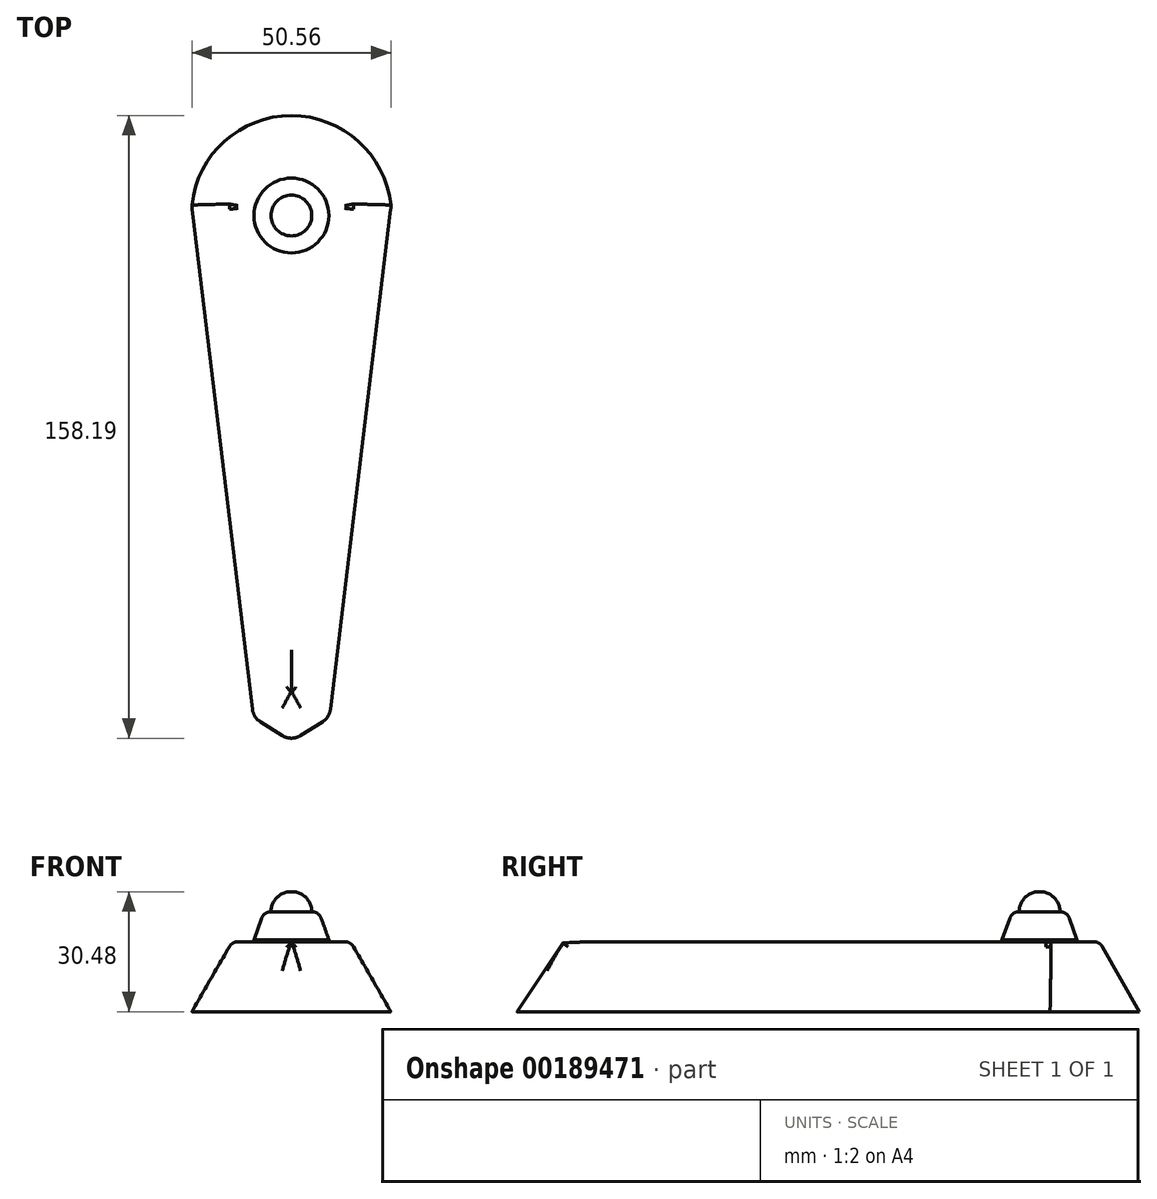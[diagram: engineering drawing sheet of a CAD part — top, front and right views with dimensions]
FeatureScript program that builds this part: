
annotation { "Feature Type Name" : "Feature", "Feature Type Description" : "" }
export const myFeature = defineFeature(function(context is Context, id is Id, definition is map)
    precondition{}
    {
        {
            var Q0;
            Q0=qCreatedBy(makeId("Top.planeOp"),FACE);
            var sketch = newSketch(context, id + "F0", { "sketchPlane" : qUnion([Q0])});
            skArc(sketch, "E0", {"start": v(25.3, 63.5) * mm, "mid": v(0, 86.74) * mm, "end": v(-25.3, 63.5) * mm});
            skLineSegment(sketch, "E1", {"start": v(-25.3, 63.5) * mm, "end": v(-9.65, -66.18) * mm});
            skLineSegment(sketch, "E2", {"start": v(25.3, 63.5) * mm, "end": v(9.65, -66.18) * mm});
            skLineSegment(sketch, "E3", {"start": v(-9.65, -66.18) * mm, "end": v(0, -72.23) * mm});
            skLineSegment(sketch, "E4", {"start": v(9.65, -66.18) * mm, "end": v(0, -72.23) * mm});
            skSolve(sketch);
        }
        {
            var Q0;
            Q0=makeQuery(id+"F0.imprint","IMPRINT",FACE,{"disambiguationData":[TD([[makeQuery(id+"F0.imprint","IMPRINT",EDGE,{"derivedFrom":sQuery(id+"F0.wireOp",EDGE,"E0")}),1.0]])]});
            extrude(context, id + "F1", {"entities" : qUnion([Q0]), "depth" : 17.78 * mm});
        }
        {
            var Q0;
            Q0=makeQuery(id+"F1.opExtrude","CAP_FACE",FACE,{"disambiguationData":[OSD([sQuery(id+"F0.wireOp",EDGE,"E0"),sQuery(id+"F0.wireOp",EDGE,"E1"),sQuery(id+"F0.wireOp",EDGE,"E2"),sQuery(id+"F0.wireOp",EDGE,"E3"),sQuery(id+"F0.wireOp",EDGE,"E4")])],"isStart":false});
            chamfer(context, id + "F2", {"entities" : qUnion([Q0]), "chamferType" : ChamferType.TWO_OFFSETS, "width1" : 10.16 * mm, "oppositeDirection" : false, "width2" : 17.78 * mm, "tangentPropagation" : true});
        }
        {
            var Q0;
            Q0=makeQuery(id+"F2.opChamfer","BLEND_EDGE",EDGE,{"blendedFrom":[makeQuery(id+"F1.opExtrude","CAP_EDGE",EDGE,{"disambiguationData":[OSD([sQuery(id+"F0.wireOp",EDGE,"E2")])],"isStart":false}),makeQuery(id+"F1.opExtrude","CAP_EDGE",EDGE,{"disambiguationData":[OSD([sQuery(id+"F0.wireOp",EDGE,"E4")])],"isStart":false})],"blendedInto":[]});
            var Q1;
            Q1=makeQuery(id+"F2.opChamfer","BLEND_EDGE",EDGE,{"blendedFrom":[makeQuery(id+"F1.opExtrude","CAP_EDGE",EDGE,{"disambiguationData":[OSD([sQuery(id+"F0.wireOp",EDGE,"E3")])],"isStart":false}),makeQuery(id+"F1.opExtrude","CAP_EDGE",EDGE,{"disambiguationData":[OSD([sQuery(id+"F0.wireOp",EDGE,"E4")])],"isStart":false})],"blendedInto":[]});
            var Q2;
            Q2=makeQuery(id+"F2.opChamfer","BLEND_EDGE",EDGE,{"blendedFrom":[makeQuery(id+"F1.opExtrude","CAP_EDGE",EDGE,{"disambiguationData":[OSD([sQuery(id+"F0.wireOp",EDGE,"E0")])],"isStart":false}),makeQuery(id+"F1.opExtrude","CAP_EDGE",EDGE,{"disambiguationData":[OSD([sQuery(id+"F0.wireOp",EDGE,"E2")])],"isStart":false})],"blendedInto":[]});
            var Q3;
            Q3=makeQuery(id+"F2.opChamfer","BLEND_EDGE",EDGE,{"blendedFrom":[makeQuery(id+"F1.opExtrude","CAP_EDGE",EDGE,{"disambiguationData":[OSD([sQuery(id+"F0.wireOp",EDGE,"E1")])],"isStart":false}),makeQuery(id+"F1.opExtrude","CAP_EDGE",EDGE,{"disambiguationData":[OSD([sQuery(id+"F0.wireOp",EDGE,"E3")])],"isStart":false})],"blendedInto":[]});
            var Q4;
            Q4=makeQuery(id+"F2.opChamfer","BLEND_EDGE",EDGE,{"blendedFrom":[makeQuery(id+"F1.opExtrude","CAP_EDGE",EDGE,{"disambiguationData":[OSD([sQuery(id+"F0.wireOp",EDGE,"E0")])],"isStart":false}),makeQuery(id+"F1.opExtrude","CAP_EDGE",EDGE,{"disambiguationData":[OSD([sQuery(id+"F0.wireOp",EDGE,"E1")])],"isStart":false})],"blendedInto":[]});
            fillet(context, id + "F3", {"entities" : qUnion([Q0, Q1, Q2, Q3, Q4]), "radius" : 5.08 * mm, "tangentPropagation" : true, "allowEdgeOverflow" : false});
        }
        {
            var Q0;
            Q0=makeQuery(id+"F1.opExtrude","CAP_FACE",FACE,{"disambiguationData":[OSD([sQuery(id+"F0.wireOp",EDGE,"E0"),sQuery(id+"F0.wireOp",EDGE,"E1"),sQuery(id+"F0.wireOp",EDGE,"E2"),sQuery(id+"F0.wireOp",EDGE,"E3"),sQuery(id+"F0.wireOp",EDGE,"E4")])],"isStart":false});
            fillet(context, id + "F4", {"entities" : qUnion([Q0]), "radius" : 2.54 * mm, "tangentPropagation" : true, "allowEdgeOverflow" : false});
        }
        {
            var Q0;
            Q0=makeQuery(id+"F1.opExtrude","CAP_FACE",FACE,{"disambiguationData":[OSD([sQuery(id+"F0.wireOp",EDGE,"E0"),sQuery(id+"F0.wireOp",EDGE,"E1"),sQuery(id+"F0.wireOp",EDGE,"E2"),sQuery(id+"F0.wireOp",EDGE,"E3"),sQuery(id+"F0.wireOp",EDGE,"E4")])],"isStart":false});
            var sketch = newSketch(context, id + "F5", { "sketchPlane" : qUnion([Q0])});
            skCircle(sketch, "E5", {"center": v(0, 61.34) * mm, "radius": 9.5 * mm});
            skSolve(sketch);
        }
        {
            var Q0;
            Q0 = qSketchRegion(id + "F5", true);
            extrude(context, id + "F6", {"entities" : qUnion([Q0]), "operationType" : NewBodyOperationType.ADD, "depth" : 7.62 * mm});
        }
        {
            var Q0;
            Q0=makeQuery(id+"F6.opExtrude","CAP_FACE",FACE,{"disambiguationData":[OSD([sQuery(id+"F5.wireOp",EDGE,"E5")])],"isStart":false});
            chamfer(context, id + "F7", {"entities" : qUnion([Q0]), "chamferType" : ChamferType.TWO_OFFSETS, "width1" : 2.54 * mm, "oppositeDirection" : false, "width2" : 7.11 * mm, "tangentPropagation" : true});
        }
        {
            var Q0;
            Q0=makeQuery(id+"F6.opExtrude","CAP_FACE",FACE,{"disambiguationData":[OSD([sQuery(id+"F5.wireOp",EDGE,"E5")])],"isStart":false});
            fillet(context, id + "F8", {"entities" : qUnion([Q0]), "radius" : 2.54 * mm, "tangentPropagation" : true, "allowEdgeOverflow" : false});
        }
        {
            var Q0;
            Q0=makeQuery(id+"F6.opExtrude","CAP_FACE",FACE,{"disambiguationData":[OSD([sQuery(id+"F5.wireOp",EDGE,"E5")])],"isStart":false});
            extrude(context, id + "F9", {"entities" : qUnion([Q0]), "operationType" : NewBodyOperationType.ADD, "depth" : 5.08 * mm});
        }
        {
            var Q0;
            Q0=makeQuery(id+"F9.opExtrude","CAP_FACE",FACE,{"disambiguationData":[OSD([sQuery(id+"F5.wireOp",EDGE,"E5")])],"isStart":false});
            fillet(context, id + "F10", {"entities" : qUnion([Q0]), "radius" : 5.08 * mm, "tangentPropagation" : true, "allowEdgeOverflow" : false});
        }
    });
